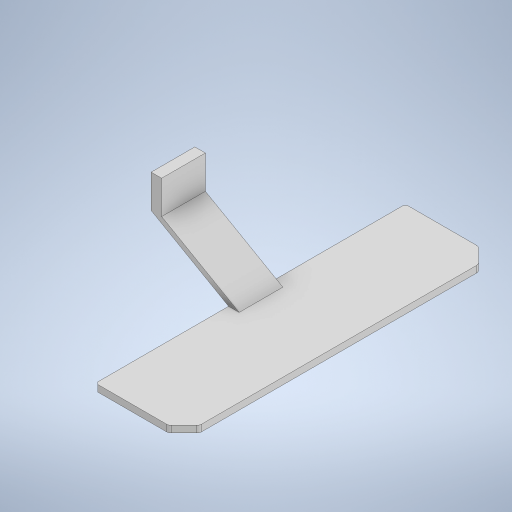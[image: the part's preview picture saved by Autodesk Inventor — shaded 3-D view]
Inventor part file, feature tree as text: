
AUTODESK INVENTOR PART (.ipt)
format: ipt  version: 2024 (Build 280153000, 153)  size: 258,048 bytes
history: native  units: in
note: dims shown in document units (in); Inventor stores cm internally (conversion verified against a paired STEP export)
features: extrude x3, sketch x3, chamfer x2, fillet x1
ambient origin geometry x8: Origin, YZ Plane, XZ Plane, XY Plane, X Axis, Y Axis, Z Axis, Center Point
bodies: Solid1 (feature_tree)
feature tree (9):
  extrude  "Extrusion1"  Depth=0.187in
  extrude  "Extrusion2"  Depth=2.3622in
  extrude  "Extrusion3"  Depth=0.0787in
  chamfer  "Chamfer1"  Distance=1.378in
  chamfer  "Chamfer2"  Distance=1.378in
  fillet  "Fillet1"  Radius=0.7776in
  sketch  "Sketch1"  dims[d0=0.7776in d1=0.187in]
  sketch  "Sketch3"  dims[d2=0.5906in d3=0.0in d4=2.3622in]
  sketch  "Sketch4"  dims[d5=2.1654in d6=1.9685in d7=1.378in d8=1.378in d9=0.7776in d10=0.0in d11=2.7559in d12=2.7559in d13=1.5748in d14=0.1181in d15=0.0in d16=0.0394in d17=0.0787in d18=45.0deg d19=0.2756in d20=0.0787in d21=45.0deg d22=0.0787in d23=0.7874in d24=0.7874in]
